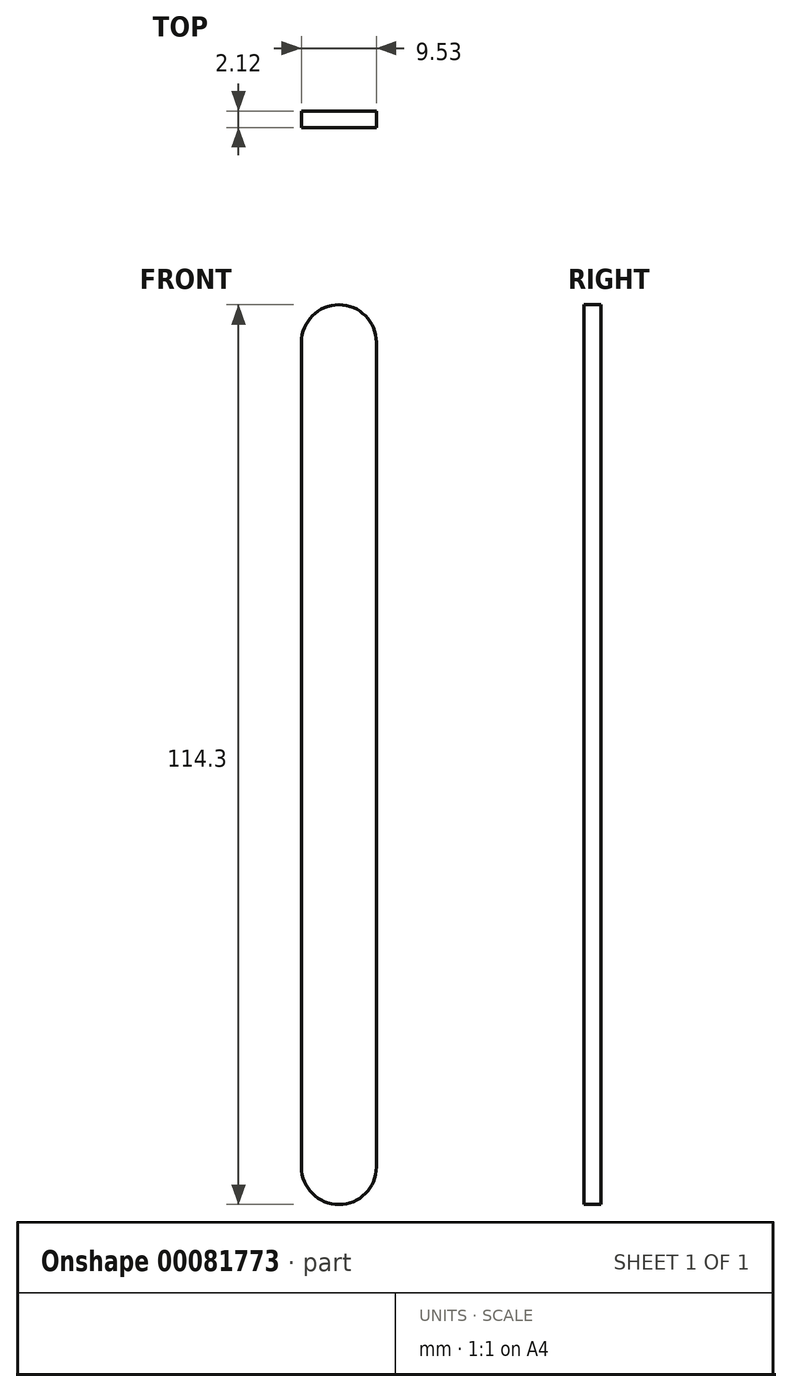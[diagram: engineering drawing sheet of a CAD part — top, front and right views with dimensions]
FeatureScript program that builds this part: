
annotation { "Feature Type Name" : "Feature", "Feature Type Description" : "" }
export const myFeature = defineFeature(function(context is Context, id is Id, definition is map)
    precondition{}
    {
        {
            var Q0;
            Q0=qCreatedBy(makeId("Front.planeOp"),FACE);
            var sketch = newSketch(context, id + "F0", { "sketchPlane" : qUnion([Q0])});
            skLineSegment(sketch, "E0.bottom", {"start": v(4.76, 0) * mm, "end": v(4.76, 0) * mm});
            skLineSegment(sketch, "E0.top", {"start": v(4.76, 114.3) * mm, "end": v(4.76, 114.3) * mm});
            skLineSegment(sketch, "E0.left", {"start": v(0, 4.76) * mm, "end": v(0, 109.54) * mm});
            skLineSegment(sketch, "E0.right", {"start": v(9.53, 4.76) * mm, "end": v(9.52, 109.54) * mm});
            skPoint(sketch, "E1.visualSharp", {"position": v(9.52, 114.3) * mm});
            skArc(sketch, "E1.filletArc", {"start": v(9.52, 109.54) * mm, "mid": v(8.13, 112.9) * mm, "end": v(4.76, 114.3) * mm});
            skPoint(sketch, "E2.visualSharp", {"position": v(9.53, 0) * mm});
            skArc(sketch, "E2.filletArc", {"start": v(4.76, 0) * mm, "mid": v(8.13, 1.4) * mm, "end": v(9.53, 4.76) * mm});
            skPoint(sketch, "E3.visualSharp", {"position": v(0, 114.3) * mm});
            skArc(sketch, "E3.filletArc", {"start": v(4.76, 114.3) * mm, "mid": v(1.4, 112.9) * mm, "end": v(0, 109.54) * mm});
            skPoint(sketch, "E4.visualSharp", {"position": v(0, 0) * mm});
            skArc(sketch, "E4.filletArc", {"start": v(0, 4.76) * mm, "mid": v(1.4, 1.4) * mm, "end": v(4.76, 0) * mm});
            skSolve(sketch);
        }
        {
            var Q0;
            Q0=makeQuery(id+"F0.imprint","IMPRINT",FACE,{"disambiguationData":[TD([[makeQuery(id+"F0.imprint","IMPRINT",EDGE,{"derivedFrom":sQuery(id+"F0.wireOp",EDGE,"E0.left")}),-1.0]])]});
            extrude(context, id + "F1", {"entities" : qUnion([Q0]), "depth" : 2.12 * mm});
        }
    });
